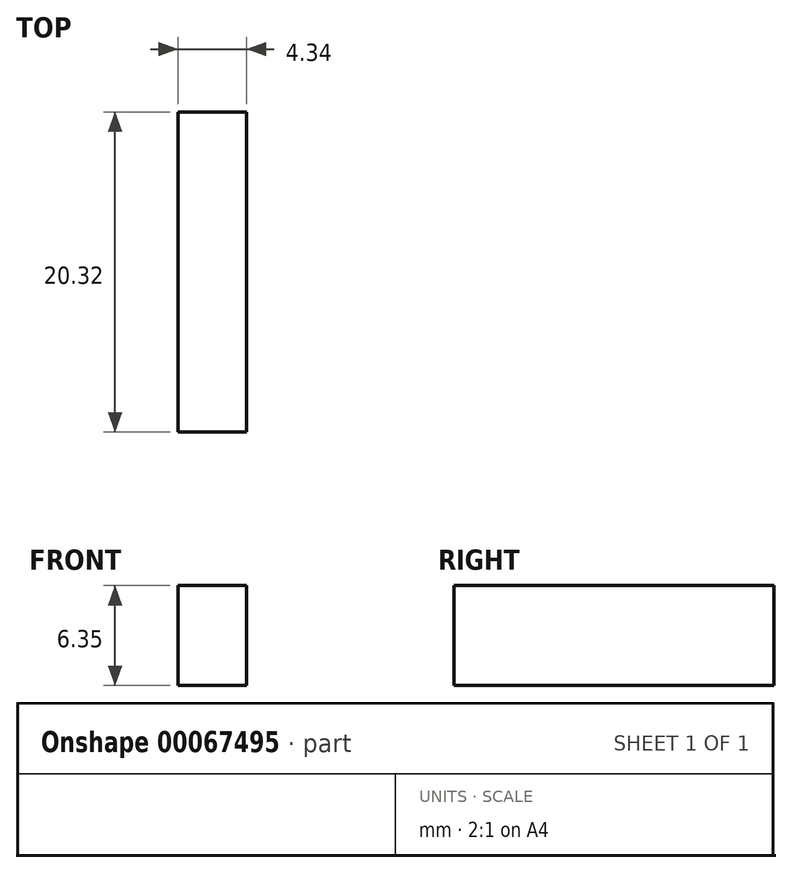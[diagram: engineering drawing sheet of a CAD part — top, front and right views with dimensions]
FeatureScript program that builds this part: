
annotation { "Feature Type Name" : "Feature", "Feature Type Description" : "" }
export const myFeature = defineFeature(function(context is Context, id is Id, definition is map)
    precondition{}
    {
        {
            var Q0;
            Q0=qCreatedBy(makeId("Right.planeOp"),FACE);
            var sketch = newSketch(context, id + "F0", { "sketchPlane" : qUnion([Q0])});
            skLineSegment(sketch, "E0.bottom", {"start": v(-17.8, 25.37) * mm, "end": v(2.51, 25.37) * mm});
            skLineSegment(sketch, "E0.top", {"start": v(-17.8, 19.02) * mm, "end": v(2.51, 19.02) * mm});
            skLineSegment(sketch, "E0.left", {"start": v(-17.8, 25.37) * mm, "end": v(-17.8, 19.02) * mm});
            skLineSegment(sketch, "E0.right", {"start": v(2.51, 25.37) * mm, "end": v(2.51, 19.02) * mm});
            skSolve(sketch);
        }
        {
            var Q0;
            Q0 = qSketchRegion(id + "F0", true);
            extrude(context, id + "F1", {"entities" : qUnion([Q0]), "depth" : 4.34 * mm});
        }
    });
